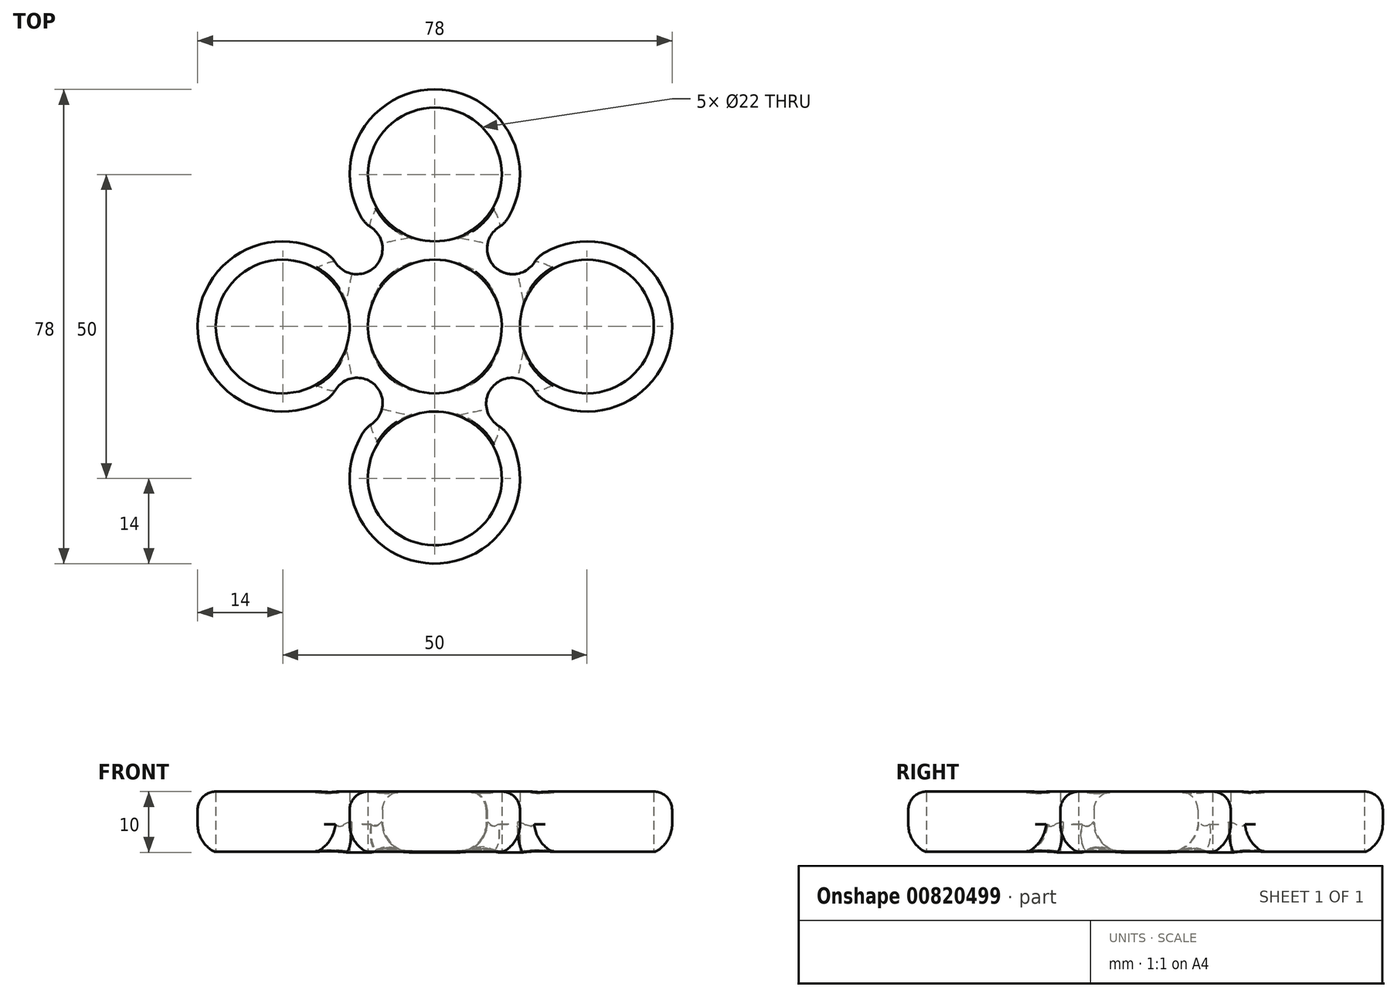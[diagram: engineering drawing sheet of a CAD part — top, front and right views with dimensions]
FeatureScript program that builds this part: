
annotation { "Feature Type Name" : "Feature", "Feature Type Description" : "" }
export const myFeature = defineFeature(function(context is Context, id is Id, definition is map)
    precondition{}
    {
        {
            var Q0;
            Q0=qCreatedBy(makeId("Top.planeOp"),FACE);
            var sketch = newSketch(context, id + "F0", { "sketchPlane" : qUnion([Q0])});
            skCircle(sketch, "E0", {"center": v(0, 0) * mm, "radius": 11 * mm});
            skCircle(sketch, "E1", {"center": v(0, 25) * mm, "radius": 11 * mm});
            skCircle(sketch, "E2", {"center": v(-25, 0) * mm, "radius": 11 * mm});
            skCircle(sketch, "E3", {"center": v(25, 0) * mm, "radius": 11 * mm});
            skCircle(sketch, "E4", {"center": v(0, -25) * mm, "radius": 11 * mm});
            skArc(sketch, "E5", {"start": v(12.15, 18.05) * mm, "mid": v(0, 39) * mm, "end": v(-12.15, 18.05) * mm});
            skArc(sketch, "E6", {"start": v(-18.05, 12.15) * mm, "mid": v(-39, 0.07) * mm, "end": v(-18.17, -12.22) * mm});
            skArc(sketch, "E7", {"start": v(18.13, -12.2) * mm, "mid": v(39, 0.05) * mm, "end": v(18.05, 12.15) * mm});
            skArc(sketch, "E8", {"start": v(-11.87, -17.58) * mm, "mid": v(-0.32, -39) * mm, "end": v(12.2, -18.13) * mm});
            skPoint(sketch, "E9.visualSharp", {"position": v(-15.1, 9.9) * mm});
            skPoint(sketch, "E10.visualSharp", {"position": v(-9.9, 15.1) * mm});
            skPoint(sketch, "E11.visualSharp", {"position": v(-15.1, -9.9) * mm});
            skPoint(sketch, "E12.visualSharp", {"position": v(9.9, -15.1) * mm});
            skPoint(sketch, "E13.visualSharp", {"position": v(15.1, -9.9) * mm});
            skPoint(sketch, "E14.visualSharp", {"position": v(15.1, 9.9) * mm});
            skPoint(sketch, "E15.visualSharp", {"position": v(9.9, 15.1) * mm});
            skArc(sketch, "E16", {"start": v(-16.33, 10.52) * mm, "mid": v(-9.83, 9.83) * mm, "end": v(-10.52, 16.33) * mm});
            skArc(sketch, "E17", {"start": v(10.52, 16.33) * mm, "mid": v(9.83, 9.83) * mm, "end": v(16.33, 10.52) * mm});
            skArc(sketch, "E18", {"start": v(16.33, -10.47) * mm, "mid": v(9.69, -9.69) * mm, "end": v(10.47, -16.33) * mm});
            skArc(sketch, "E19", {"start": v(-10.43, -16.08) * mm, "mid": v(-9.88, -9.6) * mm, "end": v(-16.34, -10.45) * mm});
            skPoint(sketch, "E20.visualSharp", {"position": v(-16.72, 11.3) * mm});
            skArc(sketch, "E20.filletArc", {"start": v(-16.33, 10.52) * mm, "mid": v(-17.1, 11.44) * mm, "end": v(-18.05, 12.15) * mm});
            skPoint(sketch, "E21.visualSharp", {"position": v(-11.3, 16.72) * mm});
            skArc(sketch, "E21.filletArc", {"start": v(-12.15, 18.05) * mm, "mid": v(-11.44, 17.1) * mm, "end": v(-10.52, 16.33) * mm});
            skPoint(sketch, "E22.visualSharp", {"position": v(-16.73, -11.3) * mm});
            skArc(sketch, "E22.filletArc", {"start": v(-18.17, -12.22) * mm, "mid": v(-17.14, -11.45) * mm, "end": v(-16.34, -10.45) * mm});
            skPoint(sketch, "E23.visualSharp", {"position": v(-11.08, -16.44) * mm});
            skArc(sketch, "E23.filletArc", {"start": v(-10.43, -16.08) * mm, "mid": v(-11.23, -16.75) * mm, "end": v(-11.87, -17.58) * mm});
            skPoint(sketch, "E24.visualSharp", {"position": v(11.3, -16.72) * mm});
            skArc(sketch, "E24.filletArc", {"start": v(12.2, -18.13) * mm, "mid": v(11.45, -17.12) * mm, "end": v(10.47, -16.33) * mm});
            skPoint(sketch, "E25.visualSharp", {"position": v(16.72, -11.3) * mm});
            skArc(sketch, "E25.filletArc", {"start": v(16.33, -10.47) * mm, "mid": v(17.12, -11.45) * mm, "end": v(18.13, -12.2) * mm});
            skPoint(sketch, "E26.visualSharp", {"position": v(16.72, 11.3) * mm});
            skArc(sketch, "E26.filletArc", {"start": v(18.05, 12.15) * mm, "mid": v(17.1, 11.44) * mm, "end": v(16.33, 10.52) * mm});
            skPoint(sketch, "E27.visualSharp", {"position": v(11.3, 16.72) * mm});
            skArc(sketch, "E27.filletArc", {"start": v(10.52, 16.33) * mm, "mid": v(11.44, 17.1) * mm, "end": v(12.15, 18.05) * mm});
            skSolve(sketch);
        }
        {
            var Q0;
            Q0=makeQuery(id+"F0.imprint","IMPRINT",FACE,{"disambiguationData":[TD([[makeQuery(id+"F0.imprint","IMPRINT",EDGE,{"derivedFrom":sQuery(id+"F0.wireOp",EDGE,"E0")}),-1.0]])]});
            extrude(context, id + "F1", {"entities" : qUnion([Q0]), "depth" : 10 * mm, "offsetDistance" : 25 * mm});
        }
        {
            var Q0;
            Q0=makeQuery(id+"F1.opExtrude","CAP_EDGE",EDGE,{"disambiguationData":[OSD([sQuery(id+"F0.wireOp",EDGE,"E6")])],"isStart":false});
            fillet(context, id + "F2", {"entities" : qUnion([Q0]), "radius" : 3 * mm, "tangentPropagation" : true, "allowEdgeOverflow" : false});
        }
        {
            var Q0;
            Q0=makeQuery(id+"F1.opExtrude","CAP_EDGE",EDGE,{"disambiguationData":[OSD([sQuery(id+"F0.wireOp",EDGE,"E8")])],"isStart":true});
            fillet(context, id + "F3", {"entities" : qUnion([Q0]), "radius" : 5 * mm, "tangentPropagation" : true, "allowEdgeOverflow" : false});
        }
        {
            var Q0;
            Q0=makeQuery(id+"F1.opExtrude","CAP_EDGE",EDGE,{"disambiguationData":[OSD([sQuery(id+"F0.wireOp",EDGE,"E2")])],"isStart":false});
            var Q1;
            Q1=makeQuery(id+"F2.opFillet","BLEND_EDGE",EDGE,{"blendedFrom":[makeQuery(id+"F1.opExtrude","CAP_EDGE",EDGE,{"disambiguationData":[OSD([sQuery(id+"F0.wireOp",EDGE,"E16")])],"isStart":false}),makeQuery(id+"F1.opExtrude","SWEPT_FACE",FACE,{"disambiguationData":[OSD([sQuery(id+"F0.wireOp",EDGE,"E2")])]})],"blendedInto":[makeQuery(id+"F1.opExtrude","SWEPT_FACE",FACE,{"disambiguationData":[OSD([sQuery(id+"F0.wireOp",EDGE,"E2")])]})]});
            var Q2;
            Q2=makeQuery(id+"F2.opFillet","BLEND_EDGE",EDGE,{"blendedFrom":[makeQuery(id+"F1.opExtrude","CAP_EDGE",EDGE,{"disambiguationData":[OSD([sQuery(id+"F0.wireOp",EDGE,"E6")])],"isStart":false}),makeQuery(id+"F1.opExtrude","SWEPT_FACE",FACE,{"disambiguationData":[OSD([sQuery(id+"F0.wireOp",EDGE,"E2")])]})],"blendedInto":[makeQuery(id+"F1.opExtrude","SWEPT_FACE",FACE,{"disambiguationData":[OSD([sQuery(id+"F0.wireOp",EDGE,"E2")])]})]});
            var Q3;
            Q3=makeQuery(id+"F2.opFillet","BLEND_EDGE",EDGE,{"blendedFrom":[makeQuery(id+"F1.opExtrude","CAP_EDGE",EDGE,{"disambiguationData":[OSD([sQuery(id+"F0.wireOp",EDGE,"E19")])],"isStart":false}),makeQuery(id+"F1.opExtrude","SWEPT_FACE",FACE,{"disambiguationData":[OSD([sQuery(id+"F0.wireOp",EDGE,"E2")])]})],"blendedInto":[makeQuery(id+"F1.opExtrude","SWEPT_FACE",FACE,{"disambiguationData":[OSD([sQuery(id+"F0.wireOp",EDGE,"E2")])]})]});
            var Q4;
            Q4=makeQuery(id+"F2.opFillet","BLEND_EDGE",EDGE,{"blendedFrom":[makeQuery(id+"F1.opExtrude","CAP_EDGE",EDGE,{"disambiguationData":[OSD([sQuery(id+"F0.wireOp",EDGE,"E5")])],"isStart":false}),makeQuery(id+"F1.opExtrude","SWEPT_FACE",FACE,{"disambiguationData":[OSD([sQuery(id+"F0.wireOp",EDGE,"E1")])]})],"blendedInto":[makeQuery(id+"F1.opExtrude","SWEPT_FACE",FACE,{"disambiguationData":[OSD([sQuery(id+"F0.wireOp",EDGE,"E1")])]})]});
            var Q5;
            Q5=makeQuery(id+"F2.opFillet","BLEND_EDGE",EDGE,{"blendedFrom":[makeQuery(id+"F1.opExtrude","CAP_EDGE",EDGE,{"disambiguationData":[OSD([sQuery(id+"F0.wireOp",EDGE,"E27.filletArc")])],"isStart":false}),makeQuery(id+"F1.opExtrude","SWEPT_FACE",FACE,{"disambiguationData":[OSD([sQuery(id+"F0.wireOp",EDGE,"E1")])]})],"blendedInto":[makeQuery(id+"F1.opExtrude","SWEPT_FACE",FACE,{"disambiguationData":[OSD([sQuery(id+"F0.wireOp",EDGE,"E1")])]})]});
            var Q6;
            Q6=makeQuery(id+"F2.opFillet","BLEND_EDGE",EDGE,{"blendedFrom":[makeQuery(id+"F1.opExtrude","CAP_EDGE",EDGE,{"disambiguationData":[OSD([sQuery(id+"F0.wireOp",EDGE,"E17")])],"isStart":false}),makeQuery(id+"F1.opExtrude","SWEPT_FACE",FACE,{"disambiguationData":[OSD([sQuery(id+"F0.wireOp",EDGE,"E1")])]})],"blendedInto":[makeQuery(id+"F1.opExtrude","SWEPT_FACE",FACE,{"disambiguationData":[OSD([sQuery(id+"F0.wireOp",EDGE,"E1")])]})]});
            var Q7;
            Q7=makeQuery(id+"F1.opExtrude","CAP_EDGE",EDGE,{"disambiguationData":[OSD([sQuery(id+"F0.wireOp",EDGE,"E1")])],"isStart":false});
            var Q8;
            Q8=makeQuery(id+"F2.opFillet","BLEND_EDGE",EDGE,{"blendedFrom":[makeQuery(id+"F1.opExtrude","CAP_EDGE",EDGE,{"disambiguationData":[OSD([sQuery(id+"F0.wireOp",EDGE,"E16")])],"isStart":false}),makeQuery(id+"F1.opExtrude","SWEPT_FACE",FACE,{"disambiguationData":[OSD([sQuery(id+"F0.wireOp",EDGE,"E1")])]})],"blendedInto":[makeQuery(id+"F1.opExtrude","SWEPT_FACE",FACE,{"disambiguationData":[OSD([sQuery(id+"F0.wireOp",EDGE,"E1")])]})]});
            var Q9;
            Q9=makeQuery(id+"F2.opFillet","BLEND_EDGE",EDGE,{"blendedFrom":[makeQuery(id+"F1.opExtrude","CAP_EDGE",EDGE,{"disambiguationData":[OSD([sQuery(id+"F0.wireOp",EDGE,"E22.filletArc")])],"isStart":false}),makeQuery(id+"F1.opExtrude","SWEPT_FACE",FACE,{"disambiguationData":[OSD([sQuery(id+"F0.wireOp",EDGE,"E2")])]})],"blendedInto":[makeQuery(id+"F1.opExtrude","SWEPT_FACE",FACE,{"disambiguationData":[OSD([sQuery(id+"F0.wireOp",EDGE,"E2")])]})]});
            var Q10;
            Q10=makeQuery(id+"F2.opFillet","BLEND_EDGE",EDGE,{"blendedFrom":[makeQuery(id+"F1.opExtrude","CAP_EDGE",EDGE,{"disambiguationData":[OSD([sQuery(id+"F0.wireOp",EDGE,"E20.filletArc")])],"isStart":false}),makeQuery(id+"F1.opExtrude","SWEPT_FACE",FACE,{"disambiguationData":[OSD([sQuery(id+"F0.wireOp",EDGE,"E2")])]})],"blendedInto":[makeQuery(id+"F1.opExtrude","SWEPT_FACE",FACE,{"disambiguationData":[OSD([sQuery(id+"F0.wireOp",EDGE,"E2")])]})]});
            var Q11;
            Q11=makeQuery(id+"F1.opExtrude","CAP_EDGE",EDGE,{"disambiguationData":[OSD([sQuery(id+"F0.wireOp",EDGE,"E0")])],"isStart":false});
            var Q12;
            Q12=makeQuery(id+"F2.opFillet","BLEND_EDGE",EDGE,{"blendedFrom":[makeQuery(id+"F1.opExtrude","CAP_EDGE",EDGE,{"disambiguationData":[OSD([sQuery(id+"F0.wireOp",EDGE,"E17")])],"isStart":false}),makeQuery(id+"F1.opExtrude","SWEPT_FACE",FACE,{"disambiguationData":[OSD([sQuery(id+"F0.wireOp",EDGE,"E3")])]})],"blendedInto":[makeQuery(id+"F1.opExtrude","SWEPT_FACE",FACE,{"disambiguationData":[OSD([sQuery(id+"F0.wireOp",EDGE,"E3")])]})]});
            var Q13;
            Q13=makeQuery(id+"F2.opFillet","BLEND_EDGE",EDGE,{"blendedFrom":[makeQuery(id+"F1.opExtrude","CAP_EDGE",EDGE,{"disambiguationData":[OSD([sQuery(id+"F0.wireOp",EDGE,"E26.filletArc")])],"isStart":false}),makeQuery(id+"F1.opExtrude","SWEPT_FACE",FACE,{"disambiguationData":[OSD([sQuery(id+"F0.wireOp",EDGE,"E3")])]})],"blendedInto":[makeQuery(id+"F1.opExtrude","SWEPT_FACE",FACE,{"disambiguationData":[OSD([sQuery(id+"F0.wireOp",EDGE,"E3")])]})]});
            var Q14;
            Q14=makeQuery(id+"F2.opFillet","BLEND_EDGE",EDGE,{"blendedFrom":[makeQuery(id+"F1.opExtrude","CAP_EDGE",EDGE,{"disambiguationData":[OSD([sQuery(id+"F0.wireOp",EDGE,"E7")])],"isStart":false}),makeQuery(id+"F1.opExtrude","SWEPT_FACE",FACE,{"disambiguationData":[OSD([sQuery(id+"F0.wireOp",EDGE,"E3")])]})],"blendedInto":[makeQuery(id+"F1.opExtrude","SWEPT_FACE",FACE,{"disambiguationData":[OSD([sQuery(id+"F0.wireOp",EDGE,"E3")])]})]});
            var Q15;
            Q15=makeQuery(id+"F1.opExtrude","CAP_EDGE",EDGE,{"disambiguationData":[OSD([sQuery(id+"F0.wireOp",EDGE,"E3")])],"isStart":false});
            var Q16;
            Q16=makeQuery(id+"F2.opFillet","BLEND_EDGE",EDGE,{"blendedFrom":[makeQuery(id+"F1.opExtrude","CAP_EDGE",EDGE,{"disambiguationData":[OSD([sQuery(id+"F0.wireOp",EDGE,"E18")])],"isStart":false}),makeQuery(id+"F1.opExtrude","SWEPT_FACE",FACE,{"disambiguationData":[OSD([sQuery(id+"F0.wireOp",EDGE,"E3")])]})],"blendedInto":[makeQuery(id+"F1.opExtrude","SWEPT_FACE",FACE,{"disambiguationData":[OSD([sQuery(id+"F0.wireOp",EDGE,"E3")])]})]});
            var Q17;
            Q17=makeQuery(id+"F2.opFillet","BLEND_EDGE",EDGE,{"blendedFrom":[makeQuery(id+"F1.opExtrude","CAP_EDGE",EDGE,{"disambiguationData":[OSD([sQuery(id+"F0.wireOp",EDGE,"E25.filletArc")])],"isStart":false}),makeQuery(id+"F1.opExtrude","SWEPT_FACE",FACE,{"disambiguationData":[OSD([sQuery(id+"F0.wireOp",EDGE,"E3")])]})],"blendedInto":[makeQuery(id+"F1.opExtrude","SWEPT_FACE",FACE,{"disambiguationData":[OSD([sQuery(id+"F0.wireOp",EDGE,"E3")])]})]});
            var Q18;
            Q18=makeQuery(id+"F2.opFillet","BLEND_EDGE",EDGE,{"blendedFrom":[makeQuery(id+"F1.opExtrude","CAP_EDGE",EDGE,{"disambiguationData":[OSD([sQuery(id+"F0.wireOp",EDGE,"E18")])],"isStart":false}),makeQuery(id+"F1.opExtrude","SWEPT_FACE",FACE,{"disambiguationData":[OSD([sQuery(id+"F0.wireOp",EDGE,"E4")])]})],"blendedInto":[makeQuery(id+"F1.opExtrude","SWEPT_FACE",FACE,{"disambiguationData":[OSD([sQuery(id+"F0.wireOp",EDGE,"E4")])]})]});
            var Q19;
            Q19=makeQuery(id+"F1.opExtrude","CAP_EDGE",EDGE,{"disambiguationData":[OSD([sQuery(id+"F0.wireOp",EDGE,"E4")])],"isStart":false});
            var Q20;
            Q20=makeQuery(id+"F2.opFillet","BLEND_EDGE",EDGE,{"blendedFrom":[makeQuery(id+"F1.opExtrude","CAP_EDGE",EDGE,{"disambiguationData":[OSD([sQuery(id+"F0.wireOp",EDGE,"E19")])],"isStart":false}),makeQuery(id+"F1.opExtrude","SWEPT_FACE",FACE,{"disambiguationData":[OSD([sQuery(id+"F0.wireOp",EDGE,"E4")])]})],"blendedInto":[makeQuery(id+"F1.opExtrude","SWEPT_FACE",FACE,{"disambiguationData":[OSD([sQuery(id+"F0.wireOp",EDGE,"E4")])]})]});
            var Q21;
            Q21=makeQuery(id+"F2.opFillet","BLEND_EDGE",EDGE,{"blendedFrom":[makeQuery(id+"F1.opExtrude","CAP_EDGE",EDGE,{"disambiguationData":[OSD([sQuery(id+"F0.wireOp",EDGE,"E8")])],"isStart":false}),makeQuery(id+"F1.opExtrude","SWEPT_FACE",FACE,{"disambiguationData":[OSD([sQuery(id+"F0.wireOp",EDGE,"E4")])]})],"blendedInto":[makeQuery(id+"F1.opExtrude","SWEPT_FACE",FACE,{"disambiguationData":[OSD([sQuery(id+"F0.wireOp",EDGE,"E4")])]})]});
            var Q22;
            Q22=makeQuery(id+"F2.opFillet","BLEND_EDGE",EDGE,{"blendedFrom":[makeQuery(id+"F1.opExtrude","CAP_EDGE",EDGE,{"disambiguationData":[OSD([sQuery(id+"F0.wireOp",EDGE,"E24.filletArc")])],"isStart":false}),makeQuery(id+"F1.opExtrude","SWEPT_FACE",FACE,{"disambiguationData":[OSD([sQuery(id+"F0.wireOp",EDGE,"E4")])]})],"blendedInto":[makeQuery(id+"F1.opExtrude","SWEPT_FACE",FACE,{"disambiguationData":[OSD([sQuery(id+"F0.wireOp",EDGE,"E4")])]})]});
            fillet(context, id + "F4", {"entities" : qUnion([Q0, Q1, Q2, Q3, Q4, Q5, Q6, Q7, Q8, Q9, Q10, Q11, Q12, Q13, Q14, Q15, Q16, Q17, Q18, Q19, Q20, Q21, Q22]), "radius" : 0.2 * mm, "tangentPropagation" : true, "allowEdgeOverflow" : false});
        }
        {
            var Q0;
            Q0=makeQuery(id+"F1.opExtrude","CAP_EDGE",EDGE,{"disambiguationData":[OSD([sQuery(id+"F0.wireOp",EDGE,"E0")])],"isStart":true});
            var Q1;
            Q1=makeQuery(id+"F1.opExtrude","CAP_EDGE",EDGE,{"disambiguationData":[OSD([sQuery(id+"F0.wireOp",EDGE,"E0")])],"isStart":true});
            var Q2;
            Q2=makeQuery(id+"F1.opExtrude","CAP_EDGE",EDGE,{"disambiguationData":[OSD([sQuery(id+"F0.wireOp",EDGE,"E0")])],"isStart":true});
            var Q3;
            Q3=makeQuery(id+"F3.opFillet","BLEND_EDGE",EDGE,{"disambiguationData":[OD(0.0)],"blendedFrom":[makeQuery(id+"F1.opExtrude","CAP_EDGE",EDGE,{"disambiguationData":[OSD([sQuery(id+"F0.wireOp",EDGE,"E19")])],"isStart":true}),makeQuery(id+"F1.opExtrude","SWEPT_FACE",FACE,{"disambiguationData":[OSD([sQuery(id+"F0.wireOp",EDGE,"E4")])]})],"blendedInto":[makeQuery(id+"F1.opExtrude","SWEPT_FACE",FACE,{"disambiguationData":[OSD([sQuery(id+"F0.wireOp",EDGE,"E4")])]})]});
            var Q4;
            Q4=makeQuery(id+"F3.opFillet","BLEND_EDGE",EDGE,{"disambiguationData":[OD(1.0)],"blendedFrom":[makeQuery(id+"F1.opExtrude","CAP_EDGE",EDGE,{"disambiguationData":[OSD([sQuery(id+"F0.wireOp",EDGE,"E19")])],"isStart":true}),makeQuery(id+"F1.opExtrude","SWEPT_FACE",FACE,{"disambiguationData":[OSD([sQuery(id+"F0.wireOp",EDGE,"E4")])]})],"blendedInto":[makeQuery(id+"F1.opExtrude","SWEPT_FACE",FACE,{"disambiguationData":[OSD([sQuery(id+"F0.wireOp",EDGE,"E4")])]})]});
            var Q5;
            Q5=makeQuery(id+"F1.opExtrude","CAP_EDGE",EDGE,{"disambiguationData":[OSD([sQuery(id+"F0.wireOp",EDGE,"E4")])],"isStart":true});
            var Q6;
            Q6=makeQuery(id+"F3.opFillet","BLEND_EDGE",EDGE,{"blendedFrom":[makeQuery(id+"F1.opExtrude","CAP_EDGE",EDGE,{"disambiguationData":[OSD([sQuery(id+"F0.wireOp",EDGE,"E18")])],"isStart":true}),makeQuery(id+"F1.opExtrude","SWEPT_FACE",FACE,{"disambiguationData":[OSD([sQuery(id+"F0.wireOp",EDGE,"E4")])]})],"blendedInto":[makeQuery(id+"F1.opExtrude","SWEPT_FACE",FACE,{"disambiguationData":[OSD([sQuery(id+"F0.wireOp",EDGE,"E4")])]})]});
            var Q7;
            Q7=makeQuery(id+"F3.opFillet","BLEND_EDGE",EDGE,{"blendedFrom":[makeQuery(id+"F1.opExtrude","CAP_EDGE",EDGE,{"disambiguationData":[OSD([sQuery(id+"F0.wireOp",EDGE,"E18")])],"isStart":true}),makeQuery(id+"F1.opExtrude","SWEPT_FACE",FACE,{"disambiguationData":[OSD([sQuery(id+"F0.wireOp",EDGE,"E0")])]})],"blendedInto":[makeQuery(id+"F1.opExtrude","SWEPT_FACE",FACE,{"disambiguationData":[OSD([sQuery(id+"F0.wireOp",EDGE,"E0")])]})]});
            var Q8;
            Q8=makeQuery(id+"F3.opFillet","BLEND_EDGE",EDGE,{"blendedFrom":[makeQuery(id+"F1.opExtrude","CAP_EDGE",EDGE,{"disambiguationData":[OSD([sQuery(id+"F0.wireOp",EDGE,"E17")])],"isStart":true}),makeQuery(id+"F1.opExtrude","SWEPT_FACE",FACE,{"disambiguationData":[OSD([sQuery(id+"F0.wireOp",EDGE,"E0")])]})],"blendedInto":[makeQuery(id+"F1.opExtrude","SWEPT_FACE",FACE,{"disambiguationData":[OSD([sQuery(id+"F0.wireOp",EDGE,"E0")])]})]});
            var Q9;
            Q9=makeQuery(id+"F3.opFillet","BLEND_EDGE",EDGE,{"blendedFrom":[makeQuery(id+"F1.opExtrude","CAP_EDGE",EDGE,{"disambiguationData":[OSD([sQuery(id+"F0.wireOp",EDGE,"E16")])],"isStart":true}),makeQuery(id+"F1.opExtrude","SWEPT_FACE",FACE,{"disambiguationData":[OSD([sQuery(id+"F0.wireOp",EDGE,"E0")])]})],"blendedInto":[makeQuery(id+"F1.opExtrude","SWEPT_FACE",FACE,{"disambiguationData":[OSD([sQuery(id+"F0.wireOp",EDGE,"E0")])]})]});
            var Q10;
            Q10=makeQuery(id+"F3.opFillet","BLEND_EDGE",EDGE,{"blendedFrom":[makeQuery(id+"F1.opExtrude","CAP_EDGE",EDGE,{"disambiguationData":[OSD([sQuery(id+"F0.wireOp",EDGE,"E19")])],"isStart":true}),makeQuery(id+"F1.opExtrude","SWEPT_FACE",FACE,{"disambiguationData":[OSD([sQuery(id+"F0.wireOp",EDGE,"E0")])]})],"blendedInto":[makeQuery(id+"F1.opExtrude","SWEPT_FACE",FACE,{"disambiguationData":[OSD([sQuery(id+"F0.wireOp",EDGE,"E0")])]})]});
            var Q11;
            Q11=makeQuery(id+"F3.opFillet","BLEND_EDGE",EDGE,{"disambiguationData":[OD(1.0)],"blendedFrom":[makeQuery(id+"F1.opExtrude","CAP_EDGE",EDGE,{"disambiguationData":[OSD([sQuery(id+"F0.wireOp",EDGE,"E18")])],"isStart":true}),makeQuery(id+"F1.opExtrude","SWEPT_FACE",FACE,{"disambiguationData":[OSD([sQuery(id+"F0.wireOp",EDGE,"E3")])]})],"blendedInto":[makeQuery(id+"F1.opExtrude","SWEPT_FACE",FACE,{"disambiguationData":[OSD([sQuery(id+"F0.wireOp",EDGE,"E3")])]})]});
            var Q12;
            Q12=makeQuery(id+"F3.opFillet","BLEND_EDGE",EDGE,{"disambiguationData":[OD(0.0)],"blendedFrom":[makeQuery(id+"F1.opExtrude","CAP_EDGE",EDGE,{"disambiguationData":[OSD([sQuery(id+"F0.wireOp",EDGE,"E18")])],"isStart":true}),makeQuery(id+"F1.opExtrude","SWEPT_FACE",FACE,{"disambiguationData":[OSD([sQuery(id+"F0.wireOp",EDGE,"E3")])]})],"blendedInto":[makeQuery(id+"F1.opExtrude","SWEPT_FACE",FACE,{"disambiguationData":[OSD([sQuery(id+"F0.wireOp",EDGE,"E3")])]})]});
            var Q13;
            Q13=makeQuery(id+"F1.opExtrude","CAP_EDGE",EDGE,{"disambiguationData":[OSD([sQuery(id+"F0.wireOp",EDGE,"E3")])],"isStart":true});
            var Q14;
            Q14=makeQuery(id+"F3.opFillet","BLEND_EDGE",EDGE,{"blendedFrom":[makeQuery(id+"F1.opExtrude","CAP_EDGE",EDGE,{"disambiguationData":[OSD([sQuery(id+"F0.wireOp",EDGE,"E17")])],"isStart":true}),makeQuery(id+"F1.opExtrude","SWEPT_FACE",FACE,{"disambiguationData":[OSD([sQuery(id+"F0.wireOp",EDGE,"E3")])]})],"blendedInto":[makeQuery(id+"F1.opExtrude","SWEPT_FACE",FACE,{"disambiguationData":[OSD([sQuery(id+"F0.wireOp",EDGE,"E3")])]})]});
            var Q15;
            Q15=makeQuery(id+"F3.opFillet","BLEND_EDGE",EDGE,{"disambiguationData":[OD(1.0)],"blendedFrom":[makeQuery(id+"F1.opExtrude","CAP_EDGE",EDGE,{"disambiguationData":[OSD([sQuery(id+"F0.wireOp",EDGE,"E16")])],"isStart":true}),makeQuery(id+"F1.opExtrude","SWEPT_FACE",FACE,{"disambiguationData":[OSD([sQuery(id+"F0.wireOp",EDGE,"E2")])]})],"blendedInto":[makeQuery(id+"F1.opExtrude","SWEPT_FACE",FACE,{"disambiguationData":[OSD([sQuery(id+"F0.wireOp",EDGE,"E2")])]})]});
            var Q16;
            Q16=makeQuery(id+"F1.opExtrude","CAP_EDGE",EDGE,{"disambiguationData":[OSD([sQuery(id+"F0.wireOp",EDGE,"E2")])],"isStart":true});
            var Q17;
            Q17=makeQuery(id+"F3.opFillet","BLEND_EDGE",EDGE,{"blendedFrom":[makeQuery(id+"F1.opExtrude","CAP_EDGE",EDGE,{"disambiguationData":[OSD([sQuery(id+"F0.wireOp",EDGE,"E19")])],"isStart":true}),makeQuery(id+"F1.opExtrude","SWEPT_FACE",FACE,{"disambiguationData":[OSD([sQuery(id+"F0.wireOp",EDGE,"E2")])]})],"blendedInto":[makeQuery(id+"F1.opExtrude","SWEPT_FACE",FACE,{"disambiguationData":[OSD([sQuery(id+"F0.wireOp",EDGE,"E2")])]})]});
            var Q18;
            Q18=makeQuery(id+"F3.opFillet","BLEND_EDGE",EDGE,{"disambiguationData":[OD(0.0)],"blendedFrom":[makeQuery(id+"F1.opExtrude","CAP_EDGE",EDGE,{"disambiguationData":[OSD([sQuery(id+"F0.wireOp",EDGE,"E16")])],"isStart":true}),makeQuery(id+"F1.opExtrude","SWEPT_FACE",FACE,{"disambiguationData":[OSD([sQuery(id+"F0.wireOp",EDGE,"E2")])]})],"blendedInto":[makeQuery(id+"F1.opExtrude","SWEPT_FACE",FACE,{"disambiguationData":[OSD([sQuery(id+"F0.wireOp",EDGE,"E2")])]})]});
            var Q19;
            Q19=makeQuery(id+"F1.opExtrude","CAP_EDGE",EDGE,{"disambiguationData":[OSD([sQuery(id+"F0.wireOp",EDGE,"E1")])],"isStart":true});
            var Q20;
            Q20=makeQuery(id+"F3.opFillet","BLEND_EDGE",EDGE,{"blendedFrom":[makeQuery(id+"F1.opExtrude","CAP_EDGE",EDGE,{"disambiguationData":[OSD([sQuery(id+"F0.wireOp",EDGE,"E16")])],"isStart":true}),makeQuery(id+"F1.opExtrude","SWEPT_FACE",FACE,{"disambiguationData":[OSD([sQuery(id+"F0.wireOp",EDGE,"E1")])]})],"blendedInto":[makeQuery(id+"F1.opExtrude","SWEPT_FACE",FACE,{"disambiguationData":[OSD([sQuery(id+"F0.wireOp",EDGE,"E1")])]})]});
            var Q21;
            Q21=makeQuery(id+"F3.opFillet","BLEND_EDGE",EDGE,{"disambiguationData":[OD(0.0)],"blendedFrom":[makeQuery(id+"F1.opExtrude","CAP_EDGE",EDGE,{"disambiguationData":[OSD([sQuery(id+"F0.wireOp",EDGE,"E17")])],"isStart":true}),makeQuery(id+"F1.opExtrude","SWEPT_FACE",FACE,{"disambiguationData":[OSD([sQuery(id+"F0.wireOp",EDGE,"E1")])]})],"blendedInto":[makeQuery(id+"F1.opExtrude","SWEPT_FACE",FACE,{"disambiguationData":[OSD([sQuery(id+"F0.wireOp",EDGE,"E1")])]})]});
            var Q22;
            Q22=makeQuery(id+"F3.opFillet","BLEND_EDGE",EDGE,{"disambiguationData":[OD(1.0)],"blendedFrom":[makeQuery(id+"F1.opExtrude","CAP_EDGE",EDGE,{"disambiguationData":[OSD([sQuery(id+"F0.wireOp",EDGE,"E17")])],"isStart":true}),makeQuery(id+"F1.opExtrude","SWEPT_FACE",FACE,{"disambiguationData":[OSD([sQuery(id+"F0.wireOp",EDGE,"E1")])]})],"blendedInto":[makeQuery(id+"F1.opExtrude","SWEPT_FACE",FACE,{"disambiguationData":[OSD([sQuery(id+"F0.wireOp",EDGE,"E1")])]})]});
            fillet(context, id + "F5", {"entities" : qUnion([Q0, Q1, Q2, Q3, Q4, Q5, Q6, Q7, Q8, Q9, Q10, Q11, Q12, Q13, Q14, Q15, Q16, Q17, Q18, Q19, Q20, Q21, Q22]), "radius" : 0.2 * mm, "tangentPropagation" : true, "allowEdgeOverflow" : false});
        }
    });
